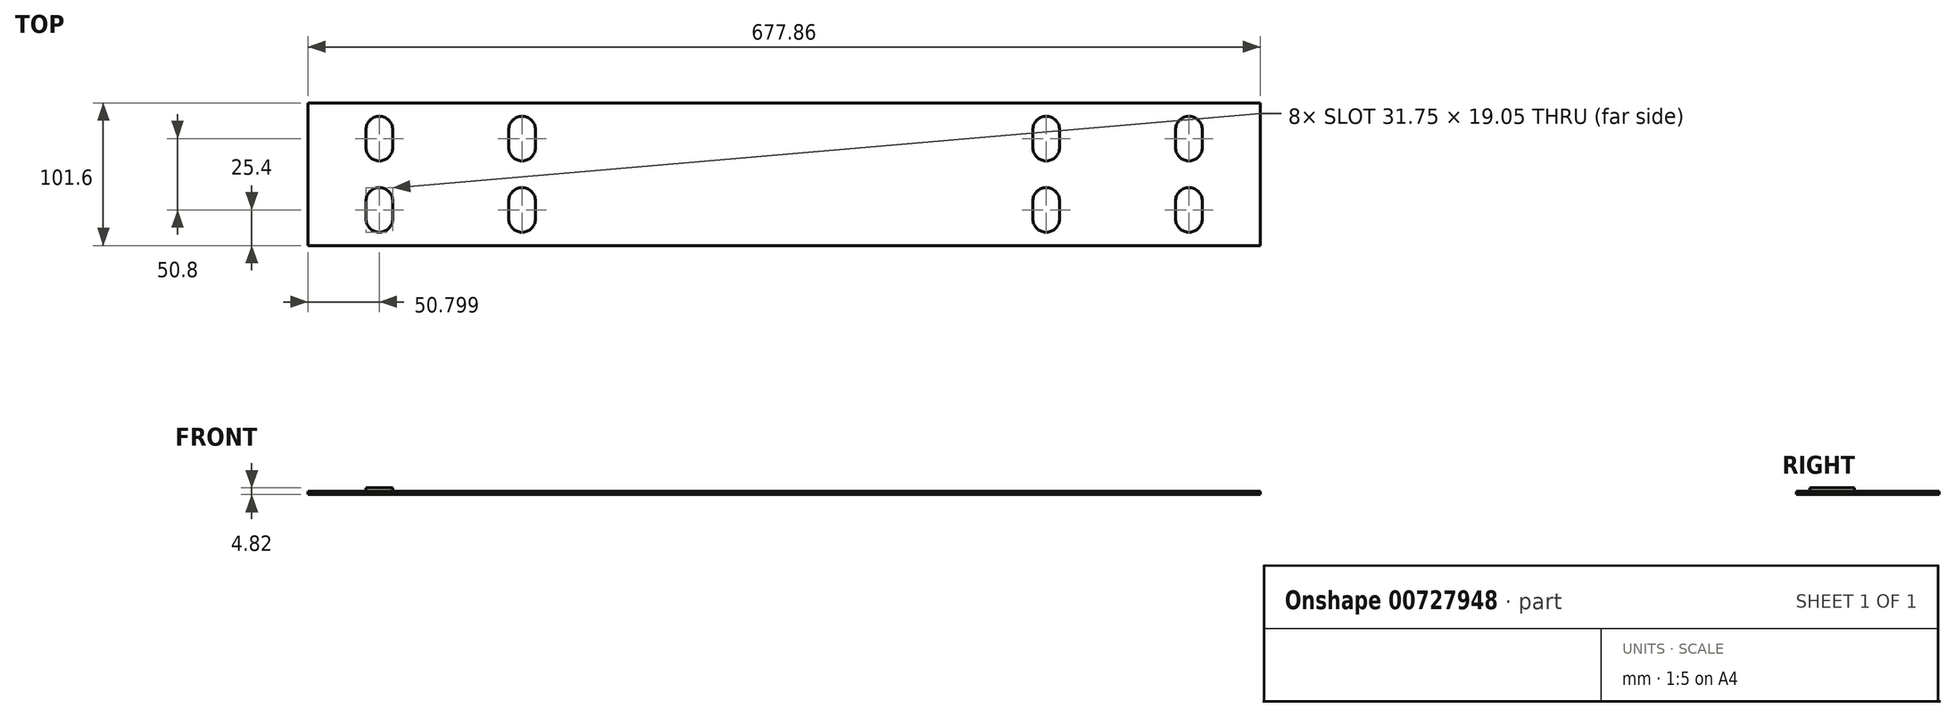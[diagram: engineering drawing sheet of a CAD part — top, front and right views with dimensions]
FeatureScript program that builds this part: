
annotation { "Feature Type Name" : "Feature", "Feature Type Description" : "" }
export const myFeature = defineFeature(function(context is Context, id is Id, definition is map)
    precondition{}
    {
        {
            var Q0;
            Q0=qCreatedBy(makeId("Top.planeOp"),FACE);
            var sketch = newSketch(context, id + "F0", { "sketchPlane" : qUnion([Q0])});
            skLineSegment(sketch, "E0.bottom", {"start": v(338.93, -50.8) * mm, "end": v(-338.93, -50.8) * mm});
            skLineSegment(sketch, "E0.top", {"start": v(338.93, 50.8) * mm, "end": v(-338.93, 50.8) * mm});
            skLineSegment(sketch, "E0.left", {"start": v(338.93, -50.8) * mm, "end": v(338.93, 50.8) * mm});
            skLineSegment(sketch, "E0.right", {"start": v(-338.93, -50.8) * mm, "end": v(-338.93, 50.8) * mm});
            skPoint(sketch, "E0.middle", {"position": v(0, 0) * mm});
            skLineSegment(sketch, "E1.MirrorCS", {"start": v(-196.06, 31.75) * mm, "end": v(-196.06, 19.05) * mm});
            skArc(sketch, "E2.MirrorCS", {"start": v(-196.06, 31.75) * mm, "mid": v(-186.53, 41.27) * mm, "end": v(-177, 31.75) * mm});
            skLineSegment(sketch, "E3.MirrorCS", {"start": v(-177, 31.75) * mm, "end": v(-177, 19.05) * mm});
            skArc(sketch, "E4.MirrorCS", {"start": v(-177, 19.05) * mm, "mid": v(-186.53, 9.52) * mm, "end": v(-196.06, 19.05) * mm});
            skArc(sketch, "E5.MirrorCS", {"start": v(-177, -19.05) * mm, "mid": v(-186.53, -9.52) * mm, "end": v(-196.06, -19.05) * mm});
            skLineSegment(sketch, "E6.MirrorCS", {"start": v(-196.06, -31.75) * mm, "end": v(-196.06, -19.05) * mm});
            skArc(sketch, "E7.MirrorCS", {"start": v(-196.06, -31.75) * mm, "mid": v(-186.53, -41.27) * mm, "end": v(-177, -31.75) * mm});
            skLineSegment(sketch, "E8.MirrorCS", {"start": v(-177, -31.75) * mm, "end": v(-177, -19.05) * mm});
            skLineSegment(sketch, "E9.MirrorCS", {"start": v(177, -31.75) * mm, "end": v(177, -19.05) * mm});
            skArc(sketch, "E10.MirrorCS", {"start": v(177, 19.05) * mm, "mid": v(186.53, 9.52) * mm, "end": v(196.06, 19.05) * mm});
            skLineSegment(sketch, "E11.MirrorCS", {"start": v(177, 31.75) * mm, "end": v(177, 19.05) * mm});
            skArc(sketch, "E12.MirrorCS", {"start": v(196.06, 31.75) * mm, "mid": v(186.53, 41.27) * mm, "end": v(177, 31.75) * mm});
            skLineSegment(sketch, "E13.MirrorCS", {"start": v(196.06, 31.75) * mm, "end": v(196.06, 19.05) * mm});
            skArc(sketch, "E14.MirrorCS", {"start": v(196.06, -31.75) * mm, "mid": v(186.53, -41.27) * mm, "end": v(177, -31.75) * mm});
            skLineSegment(sketch, "E15.MirrorCS", {"start": v(196.06, -31.75) * mm, "end": v(196.06, -19.05) * mm});
            skArc(sketch, "E16.MirrorCS", {"start": v(177, -19.05) * mm, "mid": v(186.53, -9.52) * mm, "end": v(196.06, -19.05) * mm});
            skLineSegment(sketch, "E17.bottom", {"start": v(338.94, 50.8) * mm, "end": v(-338.94, 50.8) * mm});
            skLineSegment(sketch, "E17.top", {"start": v(338.94, -50.8) * mm, "end": v(-338.94, -50.8) * mm});
            skLineSegment(sketch, "E17.left", {"start": v(338.94, 50.8) * mm, "end": v(338.94, -50.8) * mm});
            skLineSegment(sketch, "E17.right", {"start": v(-338.94, 50.8) * mm, "end": v(-338.94, -50.8) * mm});
            skPoint(sketch, "E17.cornerSnap0", {"position": v(281.77, 50.8) * mm});
            skArc(sketch, "E18.MirrorCS", {"start": v(-297.66, 19.05) * mm, "mid": v(-288.13, 9.52) * mm, "end": v(-278.6, 19.05) * mm});
            skLineSegment(sketch, "E19.MirrorCS", {"start": v(-297.66, 31.75) * mm, "end": v(-297.66, 19.05) * mm});
            skArc(sketch, "E20.MirrorCS", {"start": v(-278.6, 31.75) * mm, "mid": v(-288.13, 41.27) * mm, "end": v(-297.66, 31.75) * mm});
            skLineSegment(sketch, "E21.MirrorCS", {"start": v(-278.6, 31.75) * mm, "end": v(-278.6, 19.05) * mm});
            skLineSegment(sketch, "E22.MirrorCS", {"start": v(-278.6, -31.75) * mm, "end": v(-278.6, -19.05) * mm});
            skArc(sketch, "E23.MirrorCS", {"start": v(-297.66, -19.05) * mm, "mid": v(-288.13, -9.52) * mm, "end": v(-278.6, -19.05) * mm});
            skLineSegment(sketch, "E24.MirrorCS", {"start": v(-297.66, -31.75) * mm, "end": v(-297.66, -19.05) * mm});
            skArc(sketch, "E25.MirrorCS", {"start": v(-278.6, -31.75) * mm, "mid": v(-288.13, -41.27) * mm, "end": v(-297.66, -31.75) * mm});
            skLineSegment(sketch, "E26.MirrorCS", {"start": v(278.6, -31.75) * mm, "end": v(278.6, -19.05) * mm});
            skLineSegment(sketch, "E27.MirrorCS", {"start": v(297.66, -31.75) * mm, "end": v(297.66, -19.05) * mm});
            skLineSegment(sketch, "E28.MirrorCS", {"start": v(297.66, 31.75) * mm, "end": v(297.66, 19.05) * mm});
            skLineSegment(sketch, "E29.MirrorCS", {"start": v(278.6, 31.75) * mm, "end": v(278.6, 19.05) * mm});
            skArc(sketch, "E30.MirrorCS", {"start": v(297.66, -19.05) * mm, "mid": v(288.13, -9.52) * mm, "end": v(278.6, -19.05) * mm});
            skArc(sketch, "E31.MirrorCS", {"start": v(278.6, -31.75) * mm, "mid": v(288.13, -41.27) * mm, "end": v(297.66, -31.75) * mm});
            skArc(sketch, "E32.MirrorCS", {"start": v(297.66, 19.05) * mm, "mid": v(288.13, 9.52) * mm, "end": v(278.6, 19.05) * mm});
            skArc(sketch, "E33.MirrorCS", {"start": v(278.6, 31.75) * mm, "mid": v(288.13, 41.27) * mm, "end": v(297.66, 31.75) * mm});
            skSolve(sketch);
        }
        {
            var Q0;
            Q0 = qSketchRegion(id + "F0", true);
            var Q1;
            Q1=makeQuery(id+"F0.imprint","IMPRINT",FACE,{"disambiguationData":[TD([[makeQuery(id+"F0.imprint","IMPRINT",EDGE,{"derivedFrom":sQuery(id+"F0.wireOp",EDGE,"2vvdnNVz-kpXw-raqR-9Y2t-eyZZvtRG7vU7")}),-1.0]])]});
            extrude(context, id + "F1", {"entities" : qUnion([Q0, Q1]), "depth" : 5.08 * mm, "offsetDistance" : 25.4 * mm});
        }
        {
            var Q0;
            Q0=makeQuery(id+"F0.imprint","IMPRINT",FACE,{"disambiguationData":[TD([[makeQuery(id+"F0.imprint","IMPRINT",EDGE,{"derivedFrom":sQuery(id+"F0.wireOp",EDGE,"E1.MirrorCS")}),-1.0]])]});
            extrude(context, id + "F2", {"entities" : qUnion([Q0]), "operationType" : NewBodyOperationType.ADD, "depth" : 5.08 * mm, "offsetDistance" : 25.4 * mm});
        }
        {
            var Q0;
            Q0=makeQuery(id+"F0.imprint","IMPRINT",FACE,{"disambiguationData":[TD([[makeQuery(id+"F0.imprint","IMPRINT",EDGE,{"derivedFrom":sQuery(id+"F0.wireOp",EDGE,"E1.MirrorCS")}),-1.0]])]});
            extrude(context, id + "F3", {"entities" : qUnion([Q0]), "operationType" : NewBodyOperationType.ADD, "oppositeDirection" : true, "depth" : 2.41 * mm, "offsetDistance" : 25.4 * mm});
        }
        {
            var Q0;
            Q0=makeQuery(id+"F0.imprint","IMPRINT",FACE,{"disambiguationData":[TD([[makeQuery(id+"F0.imprint","IMPRINT",EDGE,{"derivedFrom":sQuery(id+"F0.wireOp",EDGE,"E0.bottom")}),-1.0]])]});
            var sketch = newSketch(context, id + "F4", { "sketchPlane" : qUnion([Q0])});
            skPoint(sketch, "E34.0", {"position": v(-332.58, -44.45) * mm});
            skPoint(sketch, "E35.0", {"position": v(332.58, 44.45) * mm});
            skLineSegment(sketch, "E36.bottom", {"start": v(-332.58, -44.45) * mm, "end": v(332.58, -44.45) * mm});
            skLineSegment(sketch, "E36.top", {"start": v(-332.58, 44.45) * mm, "end": v(332.58, 44.45) * mm});
            skLineSegment(sketch, "E36.left", {"start": v(-332.58, -44.45) * mm, "end": v(-332.58, 44.45) * mm});
            skLineSegment(sketch, "E36.right", {"start": v(332.58, -44.45) * mm, "end": v(332.58, 44.45) * mm});
            skSolve(sketch);
        }
        {
            var Q0;
            Q0 = qSketchRegion(id + "F4", true);
            extrude(context, id + "F5", {"entities" : qUnion([Q0]), "operationType" : NewBodyOperationType.ADD, "depth" : 2.41 * mm, "offsetDistance" : 25.4 * mm});
        }
        {
            var Q0;
            Q0=makeQuery(id+"F0.imprint","IMPRINT",FACE,{"disambiguationData":[TD([[makeQuery(id+"F0.imprint","IMPRINT",EDGE,{"derivedFrom":sQuery(id+"F0.wireOp",EDGE,"E10.MirrorCS")}),1.0]])]});
            var Q1;
            Q1=makeQuery(id+"F0.imprint","IMPRINT",FACE,{"disambiguationData":[TD([[makeQuery(id+"F0.imprint","IMPRINT",EDGE,{"derivedFrom":sQuery(id+"F0.wireOp",EDGE,"E28.MirrorCS")}),-1.0]])]});
            var Q2;
            Q2=makeQuery(id+"F0.imprint","IMPRINT",FACE,{"disambiguationData":[TD([[makeQuery(id+"F0.imprint","IMPRINT",EDGE,{"derivedFrom":sQuery(id+"F0.wireOp",EDGE,"E26.MirrorCS")}),-1.0]])]});
            var Q3;
            Q3=makeQuery(id+"F0.imprint","IMPRINT",FACE,{"disambiguationData":[TD([[makeQuery(id+"F0.imprint","IMPRINT",EDGE,{"derivedFrom":sQuery(id+"F0.wireOp",EDGE,"E9.MirrorCS")}),-1.0]])]});
            var Q4;
            Q4=makeQuery(id+"F0.imprint","IMPRINT",FACE,{"disambiguationData":[TD([[makeQuery(id+"F0.imprint","IMPRINT",EDGE,{"derivedFrom":sQuery(id+"F0.wireOp",EDGE,"E5.MirrorCS")}),1.0]])]});
            var Q5;
            Q5=makeQuery(id+"F0.imprint","IMPRINT",FACE,{"disambiguationData":[TD([[makeQuery(id+"F0.imprint","IMPRINT",EDGE,{"derivedFrom":sQuery(id+"F0.wireOp",EDGE,"E23.MirrorCS")}),-1.0]])]});
            var Q6;
            Q6=makeQuery(id+"F0.imprint","IMPRINT",FACE,{"disambiguationData":[TD([[makeQuery(id+"F0.imprint","IMPRINT",EDGE,{"derivedFrom":sQuery(id+"F0.wireOp",EDGE,"E18.MirrorCS")}),1.0]])]});
            var Q7;
            Q7=makeQuery(id+"F0.imprint","IMPRINT",FACE,{"disambiguationData":[TD([[makeQuery(id+"F0.imprint","IMPRINT",EDGE,{"derivedFrom":sQuery(id+"F0.wireOp",EDGE,"E1.MirrorCS")}),1.0]])]});
            extrude(context, id + "F6", {"entities" : qUnion([Q0, Q1, Q2, Q3, Q4, Q5, Q6, Q7]), "operationType" : NewBodyOperationType.REMOVE, "depth" : 25.4 * mm, "offsetDistance" : 25.4 * mm});
        }
    });
